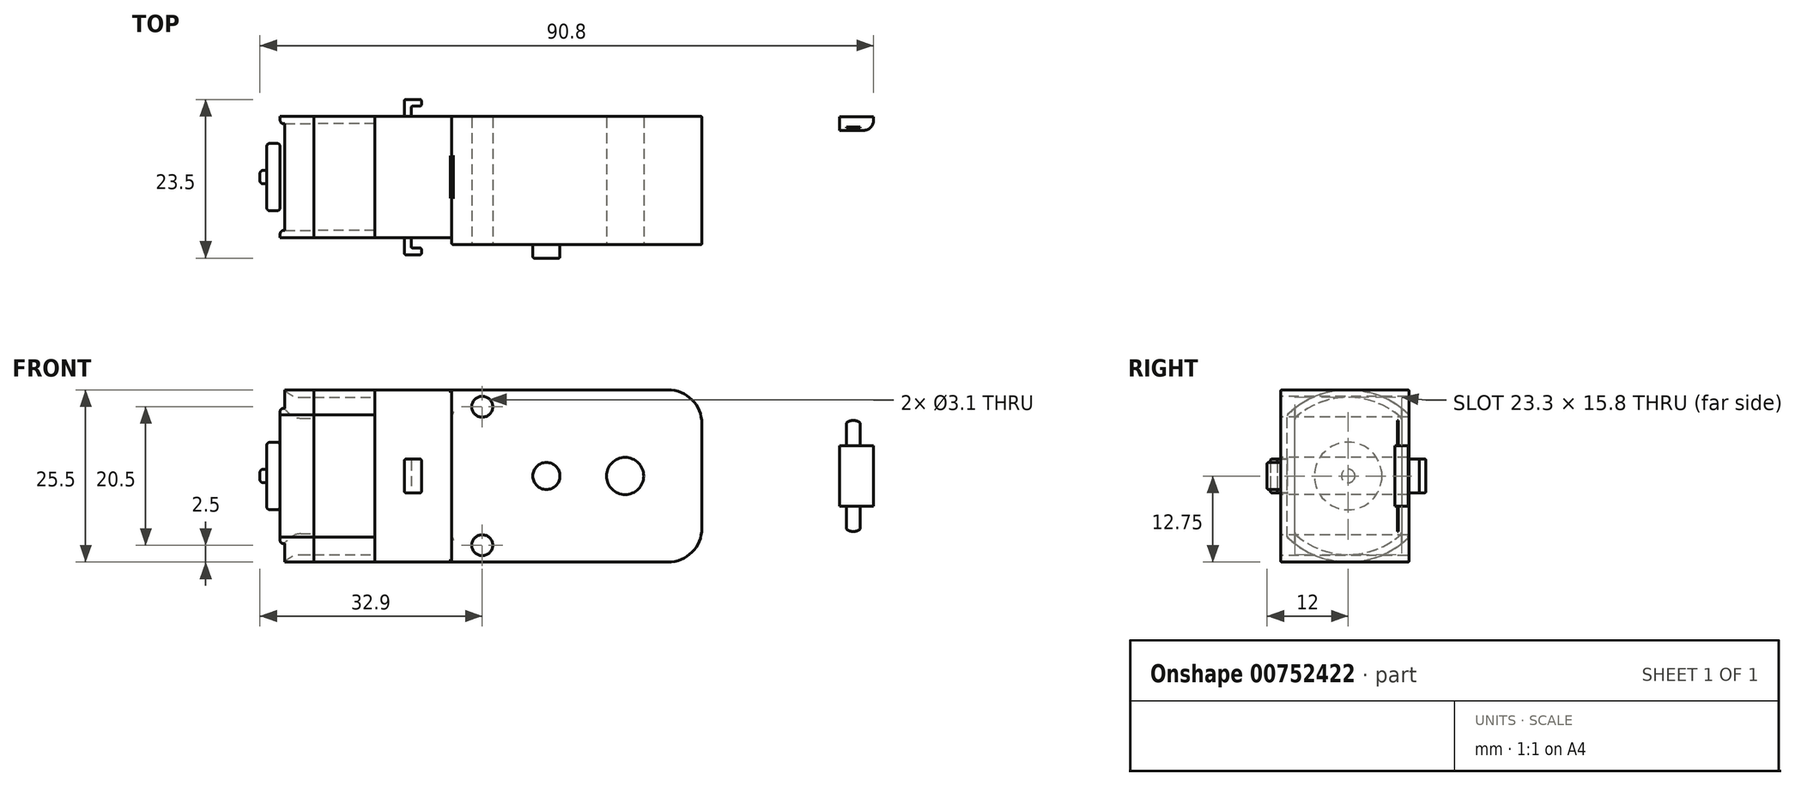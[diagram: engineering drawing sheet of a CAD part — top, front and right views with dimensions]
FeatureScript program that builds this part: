
annotation { "Feature Type Name" : "Feature", "Feature Type Description" : "" }
export const myFeature = defineFeature(function(context is Context, id is Id, definition is map)
    precondition{}
    {
        {
            var Q0;
            Q0=qCreatedBy(makeId("Front.planeOp"),FACE);
            var sketch = newSketch(context, id + "F0", { "sketchPlane" : qUnion([Q0])});
            skLineSegment(sketch, "E0.bottom", {"start": v(-18.5, 12.75) * mm, "end": v(18.5, 12.75) * mm});
            skLineSegment(sketch, "E0.top", {"start": v(-18.5, -12.75) * mm, "end": v(18.5, -12.75) * mm});
            skLineSegment(sketch, "E0.left", {"start": v(-18.5, 12.75) * mm, "end": v(-18.5, -12.75) * mm});
            skLineSegment(sketch, "E0.right", {"start": v(18.5, 12.75) * mm, "end": v(18.5, -12.75) * mm});
            skPoint(sketch, "E0.middle", {"position": v(0, 0) * mm});
            skSolve(sketch);
        }
        {
            var Q0;
            Q0=makeQuery(id+"F0.imprint","IMPRINT",FACE,{"disambiguationData":[TD([[makeQuery(id+"F0.imprint","IMPRINT",EDGE,{"derivedFrom":sQuery(id+"F0.wireOp",EDGE,"E0.bottom")}),-1.0]])]});
            extrude(context, id + "F1", {"entities" : qUnion([Q0]), "depth" : 19 * mm, "offsetDistance" : 25 * mm});
        }
        {
            var Q0;
            Q0=makeQuery(id+"F1.opExtrude","SWEPT_EDGE",EDGE,{"disambiguationData":[OSD([sQuery(id+"F0.wireOp",EDGE,"E0.bottom"),sQuery(id+"F0.wireOp",EDGE,"E0.right")])]});
            var Q1;
            Q1=makeQuery(id+"F1.opExtrude","SWEPT_EDGE",EDGE,{"disambiguationData":[OSD([sQuery(id+"F0.wireOp",EDGE,"E0.top"),sQuery(id+"F0.wireOp",EDGE,"E0.right")])]});
            fillet(context, id + "F2", {"entities" : qUnion([Q0, Q1]), "radius" : 5 * mm, "tangentPropagation" : true, "allowEdgeOverflow" : false});
        }
        {
            var Q0;
            Q0=makeQuery(id+"F1.opExtrude","SWEPT_FACE",FACE,{"disambiguationData":[OSD([sQuery(id+"F0.wireOp",EDGE,"E0.left")])]});
            var sketch = newSketch(context, id + "F3", { "sketchPlane" : qUnion([Q0])});
            skArc(sketch, "E1", {"start": v(0, 9.03) * mm, "mid": v(9, 12.75) * mm, "end": v(18, 9.03) * mm});
            skArc(sketch, "E2", {"start": v(0, -9.03) * mm, "mid": v(9, -12.75) * mm, "end": v(18, -9.03) * mm});
            skLineSegment(sketch, "E3", {"start": v(0, -9.03) * mm, "end": v(0, 9.03) * mm});
            skLineSegment(sketch, "E4", {"start": v(18, -9.03) * mm, "end": v(18, 9.03) * mm});
            skSolve(sketch);
        }
        {
            var Q0;
            {var subQ4=sQuery(id+"F3.wireOp",EDGE,"E3");Q0=makeQuery(id+"F3.imprint","IMPRINT",FACE,{"disambiguationData":[TD([[makeQuery(id+"F3.imprint","IMPRINT",EDGE,{"derivedFrom":subQ4}),1.0]])]});}
            extrude(context, id + "F4", {"entities" : qUnion([Q0]), "operationType" : NewBodyOperationType.ADD, "depth" : 11.4 * mm, "offsetDistance" : 25 * mm});
        }
        {
            var Q0;
            Q0=makeQuery(id+"F4.opExtrude","CAP_FACE",FACE,{"disambiguationData":[OSD([sQuery(id+"F3.wireOp",EDGE,"E1"),sQuery(id+"F3.wireOp",EDGE,"E2"),sQuery(id+"F3.wireOp",EDGE,"E3"),sQuery(id+"F3.wireOp",EDGE,"E4")])],"isStart":false});
            var sketch = newSketch(context, id + "F5", { "sketchPlane" : qUnion([Q0])});
            skArc(sketch, "E5.0", {"start": v(1.1, 8.56) * mm, "mid": v(9, 11.65) * mm, "end": v(16.9, 8.56) * mm});
            skLineSegment(sketch, "E5.1", {"start": v(1.1, 8.56) * mm, "end": v(1.1, -8.56) * mm});
            skArc(sketch, "E5.2", {"start": v(1.1, -8.56) * mm, "mid": v(9, -11.65) * mm, "end": v(16.9, -8.56) * mm});
            skLineSegment(sketch, "E5.3", {"start": v(16.9, -8.56) * mm, "end": v(16.9, 8.56) * mm});
            skSolve(sketch);
        }
        {
            var Q0;
            Q0=makeQuery(id+"F5.imprint","IMPRINT",FACE,{"disambiguationData":[TD([[makeQuery(id+"F5.imprint","IMPRINT",EDGE,{"derivedFrom":sQuery(id+"F5.wireOp",EDGE,"E5.0")}),-1.0]])]});
            extrude(context, id + "F6", {"entities" : qUnion([Q0]), "depth" : 9 * mm, "offsetDistance" : 25 * mm});
        }
        {
            var Q0;
            Q0=makeQuery(id+"F6.opExtrude","CAP_FACE",FACE,{"disambiguationData":[OSD([sQuery(id+"F5.wireOp",EDGE,"E5.0"),sQuery(id+"F5.wireOp",EDGE,"E5.1"),sQuery(id+"F5.wireOp",EDGE,"E5.2"),sQuery(id+"F5.wireOp",EDGE,"E5.3")])],"isStart":false});
            extrude(context, id + "F7", {"entities" : qUnion([Q0]), "depth" : 5 * mm, "offsetDistance" : 25 * mm});
        }
        {
            var Q0;
            Q0=makeQuery(id+"F7.opExtrude","CAP_EDGE",EDGE,{"disambiguationData":[OSD([sQuery(id+"F5.wireOp",EDGE,"E5.0")])],"isStart":false});
            var Q1;
            Q1=makeQuery(id+"F7.opExtrude","CAP_EDGE",EDGE,{"disambiguationData":[OSD([sQuery(id+"F5.wireOp",EDGE,"E5.2")])],"isStart":false});
            fillet(context, id + "F8", {"entities" : qUnion([Q0, Q1]), "radius" : 3 * mm, "tangentPropagation" : true, "allowEdgeOverflow" : false});
        }
        {
            var Q0;
            Q0=makeQuery(id+"F7.opExtrude","CAP_FACE",FACE,{"disambiguationData":[OSD([sQuery(id+"F5.wireOp",EDGE,"E5.0"),sQuery(id+"F5.wireOp",EDGE,"E5.1"),sQuery(id+"F5.wireOp",EDGE,"E5.2"),sQuery(id+"F5.wireOp",EDGE,"E5.3")])],"isStart":false});
            var sketch = newSketch(context, id + "F9", { "sketchPlane" : qUnion([Q0])});
            skCircle(sketch, "E6", {"center": v(9, 0) * mm, "radius": 5 * mm});
            skSolve(sketch);
        }
        {
            var Q0;
            Q0=makeQuery(id+"F9.imprint","IMPRINT",FACE,{"disambiguationData":[TD([[makeQuery(id+"F9.imprint","IMPRINT",EDGE,{"derivedFrom":sQuery(id+"F9.wireOp",EDGE,"E6")}),1.0]])]});
            extrude(context, id + "F10", {"entities" : qUnion([Q0]), "operationType" : NewBodyOperationType.ADD, "depth" : 2 * mm, "offsetDistance" : 25 * mm});
        }
        {
            var Q0;
            Q0=makeQuery(id+"F10.opExtrude","CAP_FACE",FACE,{"disambiguationData":[OSD([sQuery(id+"F9.wireOp",EDGE,"E6")])],"isStart":false});
            var sketch = newSketch(context, id + "F11", { "sketchPlane" : qUnion([Q0])});
            skCircle(sketch, "E7", {"center": v(9, 0) * mm, "radius": 1 * mm});
            skSolve(sketch);
        }
        {
            var Q0;
            Q0=makeQuery(id+"F11.imprint","IMPRINT",FACE,{"disambiguationData":[TD([[makeQuery(id+"F11.imprint","IMPRINT",EDGE,{"derivedFrom":sQuery(id+"F11.wireOp",EDGE,"E7")}),1.0]])]});
            extrude(context, id + "F12", {"entities" : qUnion([Q0]), "depth" : 1 * mm, "offsetDistance" : 25 * mm});
        }
        {
            var Q0;
            Q0=makeQuery(id+"F12.opExtrude","CAP_EDGE",EDGE,{"disambiguationData":[OSD([sQuery(id+"F11.wireOp",EDGE,"E7")])],"isStart":false});
            var Q1;
            Q1=makeQuery(id+"F10.opExtrude","CAP_EDGE",EDGE,{"disambiguationData":[OSD([sQuery(id+"F9.wireOp",EDGE,"E6")])],"isStart":false});
            var Q2;
            Q2=makeQuery(id+"F10.opExtrude","CAP_EDGE",EDGE,{"disambiguationData":[OSD([sQuery(id+"F9.wireOp",EDGE,"E6")])],"isStart":true});
            var Q3;
            Q3=makeQuery(id+"F7.opExtrude","CAP_EDGE",EDGE,{"disambiguationData":[OSD([sQuery(id+"F5.wireOp",EDGE,"E5.3")])],"isStart":false});
            var Q4;
            Q4=makeQuery(id+"F7.opExtrude","CAP_EDGE",EDGE,{"disambiguationData":[OSD([sQuery(id+"F5.wireOp",EDGE,"E5.1")])],"isStart":false});
            var Q5;
            Q5=makeQuery(id+"F6.opExtrude","SWEPT_EDGE",EDGE,{"disambiguationData":[OSD([sQuery(id+"F5.wireOp",EDGE,"E5.0"),sQuery(id+"F5.wireOp",EDGE,"E5.3")])]});
            var Q6;
            Q6=makeQuery(id+"F6.opExtrude","SWEPT_EDGE",EDGE,{"disambiguationData":[OSD([sQuery(id+"F5.wireOp",EDGE,"E5.0"),sQuery(id+"F5.wireOp",EDGE,"E5.1")])]});
            var Q7;
            Q7=makeQuery(id+"F6.opExtrude","SWEPT_EDGE",EDGE,{"disambiguationData":[OSD([sQuery(id+"F5.wireOp",EDGE,"E5.2"),sQuery(id+"F5.wireOp",EDGE,"E5.3")])]});
            var Q8;
            Q8=makeQuery(id+"F6.opExtrude","SWEPT_EDGE",EDGE,{"disambiguationData":[OSD([sQuery(id+"F5.wireOp",EDGE,"E5.1"),sQuery(id+"F5.wireOp",EDGE,"E5.2")])]});
            fillet(context, id + "F13", {"entities" : qUnion([Q0, Q1, Q2, Q3, Q4, Q5, Q6, Q7, Q8]), "radius" : 0.5 * mm, "tangentPropagation" : true, "allowEdgeOverflow" : false});
        }
        {
            var Q0;
            Q0=makeQuery(id+"F7.opExtrude","CAP_FACE",FACE,{"disambiguationData":[OSD([sQuery(id+"F5.wireOp",EDGE,"E5.0"),sQuery(id+"F5.wireOp",EDGE,"E5.1"),sQuery(id+"F5.wireOp",EDGE,"E5.2"),sQuery(id+"F5.wireOp",EDGE,"E5.3")])],"isStart":false});
            var sketch = newSketch(context, id + "F14", { "sketchPlane" : qUnion([Q0])});
            skArc(sketch, "E8", {"start": v(7.5, 9.65) * mm, "mid": v(9, 8.15) * mm, "end": v(10.5, 9.65) * mm});
            skArc(sketch, "E9", {"start": v(7.5, 11.55) * mm, "mid": v(9, 11.65) * mm, "end": v(10.5, 11.55) * mm});
            skLineSegment(sketch, "E10", {"start": v(7.5, 9.65) * mm, "end": v(7.5, 11.55) * mm});
            skLineSegment(sketch, "E11", {"start": v(10.5, 9.65) * mm, "end": v(10.5, 11.55) * mm});
            skLineSegment(sketch, "E12.MirrorCS", {"start": v(10.5, -9.65) * mm, "end": v(10.5, -11.55) * mm});
            skArc(sketch, "E13.MirrorCS", {"start": v(7.5, -9.65) * mm, "mid": v(9, -8.15) * mm, "end": v(10.5, -9.65) * mm});
            skLineSegment(sketch, "E14.MirrorCS", {"start": v(7.5, -9.65) * mm, "end": v(7.5, -11.55) * mm});
            skArc(sketch, "E15.MirrorCS", {"start": v(7.5, -11.55) * mm, "mid": v(9, -11.65) * mm, "end": v(10.5, -11.55) * mm});
            skSolve(sketch);
        }
        {
            var Q0;
            Q0=makeQuery(id+"F14.imprint","IMPRINT",FACE,{"disambiguationData":[TD([[makeQuery(id+"F14.imprint","IMPRINT",EDGE,{"derivedFrom":sQuery(id+"F14.wireOp",EDGE,"E9")}),-1.0]])]});
            var Q1;
            {var subQ0=sQuery(id+"F14.wireOp",EDGE,"E8");var subQ1=sQuery(id+"F5.wireOp",EDGE,"E5.0");var subQ2=makeQuery(id+"F8.opFillet","BLEND_EDGE",EDGE,{"blendedFrom":[makeQuery(id+"F7.opExtrude","CAP_EDGE",EDGE,{"disambiguationData":[OSD([subQ1])],"isStart":false}),makeQuery(id+"F7.opExtrude","CAP_FACE",FACE,{"disambiguationData":[OSD([subQ1,sQuery(id+"F5.wireOp",EDGE,"E5.1"),sQuery(id+"F5.wireOp",EDGE,"E5.2"),sQuery(id+"F5.wireOp",EDGE,"E5.3")])],"isStart":false})],"blendedInto":[makeQuery(id+"F7.opExtrude","CAP_FACE",FACE,{"disambiguationData":[OSD([subQ1,sQuery(id+"F5.wireOp",EDGE,"E5.1"),sQuery(id+"F5.wireOp",EDGE,"E5.2"),sQuery(id+"F5.wireOp",EDGE,"E5.3")])],"isStart":false})]});var subQ3=makeQuery(id+"F14.imprint","INTERSECT",VERTEX,{"disambiguationData":[OD(0.0)],"derivedFrom":[subQ2,subQ0]});Q1=makeQuery(id+"F14.imprint","IMPRINT",FACE,{"disambiguationData":[TD([[makeQuery(id+"F14.imprint","IMPRINT",EDGE,{"disambiguationData":[TD([[subQ3,-1.0]])],"derivedFrom":subQ0}),1.0]])]});}
            var Q2;
            {var subQ2=sQuery(id+"F14.wireOp",EDGE,"E12.MirrorCS");Q2=makeQuery(id+"F14.imprint","IMPRINT",FACE,{"disambiguationData":[TD([[makeQuery(id+"F14.imprint","IMPRINT",EDGE,{"derivedFrom":subQ2}),-1.0]])]});}
            var Q3;
            {var subQ0=sQuery(id+"F14.wireOp",EDGE,"E13.MirrorCS");var subQ1=sQuery(id+"F5.wireOp",EDGE,"E5.2");var subQ2=makeQuery(id+"F8.opFillet","BLEND_EDGE",EDGE,{"blendedFrom":[makeQuery(id+"F7.opExtrude","CAP_EDGE",EDGE,{"disambiguationData":[OSD([subQ1])],"isStart":false}),makeQuery(id+"F7.opExtrude","CAP_FACE",FACE,{"disambiguationData":[OSD([sQuery(id+"F5.wireOp",EDGE,"E5.0"),sQuery(id+"F5.wireOp",EDGE,"E5.1"),subQ1,sQuery(id+"F5.wireOp",EDGE,"E5.3")])],"isStart":false})],"blendedInto":[makeQuery(id+"F7.opExtrude","CAP_FACE",FACE,{"disambiguationData":[OSD([sQuery(id+"F5.wireOp",EDGE,"E5.0"),sQuery(id+"F5.wireOp",EDGE,"E5.1"),subQ1,sQuery(id+"F5.wireOp",EDGE,"E5.3")])],"isStart":false})]});var subQ3=makeQuery(id+"F14.imprint","INTERSECT",VERTEX,{"disambiguationData":[OD(0.0)],"derivedFrom":[subQ2,subQ0]});Q3=makeQuery(id+"F14.imprint","IMPRINT",FACE,{"disambiguationData":[TD([[makeQuery(id+"F14.imprint","IMPRINT",EDGE,{"disambiguationData":[TD([[subQ3,-1.0]])],"derivedFrom":subQ0}),-1.0]])]});}
            extrude(context, id + "F15", {"entities" : qUnion([Q0, Q1, Q2, Q3]), "operationType" : NewBodyOperationType.REMOVE, "oppositeDirection" : true, "depth" : 6 * mm, "offsetDistance" : 25 * mm});
        }
        {
            var Q0;
            Q0=makeQuery(id+"F7.opExtrude","SWEPT_FACE",FACE,{"disambiguationData":[OSD([sQuery(id+"F5.wireOp",EDGE,"E5.1")])]});
            var sketch = newSketch(context, id + "F16", { "sketchPlane" : qUnion([Q0])});
            skLineSegment(sketch, "E16", {"start": v(38.9, -4.5) * mm, "end": v(38.9, 4.5) * mm});
            skLineSegment(sketch, "E17", {"start": v(38.9, 4.5) * mm, "end": v(43.9, 4.5) * mm});
            skLineSegment(sketch, "E18", {"start": v(43.9, 4.5) * mm, "end": v(43.9, -4.5) * mm});
            skLineSegment(sketch, "E19", {"start": v(43.9, -4.5) * mm, "end": v(38.9, -4.5) * mm});
            skSolve(sketch);
        }
        {
            var Q0;
            {var subQ5=sQuery(id+"F16.wireOp",EDGE,"E16");Q0=makeQuery(id+"F16.imprint","IMPRINT",FACE,{"disambiguationData":[TD([[makeQuery(id+"F16.imprint","IMPRINT",EDGE,{"derivedFrom":subQ5}),1.0]])]});}
            var Q1;
            {var subQ1=sQuery(id+"F16.wireOp",EDGE,"E18");Q1=makeQuery(id+"F16.imprint","IMPRINT",FACE,{"disambiguationData":[TD([[makeQuery(id+"F16.imprint","IMPRINT",EDGE,{"derivedFrom":subQ1}),-1.0]])]});}
            extrude(context, id + "F17", {"entities" : qUnion([Q0, Q1]), "endBound" : BoundingType.SYMMETRIC, "depth" : 2 * mm, "offsetDistance" : 25 * mm});
        }
        {
            var Q0;
            Q0=makeQuery(id+"F17.opExtrude","CAP_EDGE",EDGE,{"disambiguationData":[OSD([sQuery(id+"F16.wireOp",EDGE,"E18")])],"isStart":false});
            fillet(context, id + "F18", {"entities" : qUnion([Q0]), "radius" : 1.5 * mm, "tangentPropagation" : true, "allowEdgeOverflow" : false});
        }
        {
            var Q0;
            Q0=makeQuery(id+"F7.opExtrude","SWEPT_FACE",FACE,{"disambiguationData":[OSD([sQuery(id+"F5.wireOp",EDGE,"E5.1")])]});
            cPlane(context, id + "F19", {"entities" : qUnion([Q0]), "cplaneType" : CPlaneType.OFFSET, "offset" : 0.5 * mm, "width" : 150 * mm, "height" : 150 * mm});
        }
        {
            var Q0;
            Q0=qCreatedBy(id+"F19.planeOp",FACE);
            var sketch = newSketch(context, id + "F20", { "sketchPlane" : qUnion([Q0])});
            skLineSegment(sketch, "E20.bottom", {"start": v(39.9, 4.5) * mm, "end": v(41.9, 4.5) * mm});
            skLineSegment(sketch, "E20.left", {"start": v(39.9, 4.5) * mm, "end": v(39.9, 7.85) * mm});
            skLineSegment(sketch, "E20.right", {"start": v(41.9, 4.5) * mm, "end": v(41.9, 7.85) * mm});
            skArc(sketch, "E21", {"start": v(41.9, 7.85) * mm, "mid": v(40.9, 8.23) * mm, "end": v(39.9, 7.85) * mm});
            skLineSegment(sketch, "E22.MirrorCS", {"start": v(39.9, -4.5) * mm, "end": v(41.9, -4.5) * mm});
            skLineSegment(sketch, "E23.MirrorCS", {"start": v(39.9, -4.5) * mm, "end": v(39.9, -7.85) * mm});
            skArc(sketch, "E24.MirrorCS", {"start": v(41.9, -7.85) * mm, "mid": v(40.9, -8.23) * mm, "end": v(39.9, -7.85) * mm});
            skLineSegment(sketch, "E25.MirrorCS", {"start": v(41.9, -4.5) * mm, "end": v(41.9, -7.85) * mm});
            skSolve(sketch);
        }
        {
            var Q0;
            Q0=makeQuery(id+"F20.imprint","IMPRINT",FACE,{"disambiguationData":[TD([[makeQuery(id+"F20.imprint","IMPRINT",EDGE,{"derivedFrom":sQuery(id+"F20.wireOp",EDGE,"E20.bottom")}),1.0]])]});
            var Q1;
            Q1=makeQuery(id+"F20.imprint","IMPRINT",FACE,{"disambiguationData":[TD([[makeQuery(id+"F20.imprint","IMPRINT",EDGE,{"derivedFrom":sQuery(id+"F20.wireOp",EDGE,"E22.MirrorCS")}),-1.0]])]});
            extrude(context, id + "F21", {"entities" : qUnion([Q0, Q1]), "depth" : 0.1 * mm, "offsetDistance" : 25 * mm});
        }
        {
            var Q0;
            Q0=makeQuery(id+"F1.opExtrude","CAP_FACE",FACE,{"disambiguationData":[OSD([sQuery(id+"F0.wireOp",EDGE,"E0.bottom"),sQuery(id+"F0.wireOp",EDGE,"E0.top"),sQuery(id+"F0.wireOp",EDGE,"E0.left"),sQuery(id+"F0.wireOp",EDGE,"E0.right")])],"isStart":false});
            var sketch = newSketch(context, id + "F22", { "sketchPlane" : qUnion([Q0])});
            skCircle(sketch, "E26", {"center": v(-4.5, 0) * mm, "radius": 2 * mm});
            skSolve(sketch);
        }
        {
            var Q0;
            Q0=makeQuery(id+"F22.imprint","IMPRINT",FACE,{"disambiguationData":[TD([[makeQuery(id+"F22.imprint","IMPRINT",EDGE,{"derivedFrom":sQuery(id+"F22.wireOp",EDGE,"E26")}),1.0]])]});
            extrude(context, id + "F23", {"entities" : qUnion([Q0]), "operationType" : NewBodyOperationType.ADD, "depth" : 2 * mm, "offsetDistance" : 25 * mm});
        }
        {
            var Q0;
            Q0=makeQuery(id+"F1.opExtrude","CAP_FACE",FACE,{"disambiguationData":[OSD([sQuery(id+"F0.wireOp",EDGE,"E0.bottom"),sQuery(id+"F0.wireOp",EDGE,"E0.top"),sQuery(id+"F0.wireOp",EDGE,"E0.left"),sQuery(id+"F0.wireOp",EDGE,"E0.right")])],"isStart":false});
            var sketch = newSketch(context, id + "F24", { "sketchPlane" : qUnion([Q0])});
            skCircle(sketch, "E27", {"center": v(7.15, 0) * mm, "radius": 2.75 * mm});
            skPoint(sketch, "E28", {"position": v(-14, 10.25) * mm});
            skPoint(sketch, "E29", {"position": v(-14, -10.25) * mm});
            skSolve(sketch);
        }
        {
            var Q0;
            Q0=makeQuery(id+"F24.imprint","IMPRINT",FACE,{"disambiguationData":[TD([[makeQuery(id+"F24.imprint","IMPRINT",EDGE,{"derivedFrom":sQuery(id+"F24.wireOp",EDGE,"E27")}),1.0]])]});
            extrude(context, id + "F25", {"entities" : qUnion([Q0]), "operationType" : NewBodyOperationType.REMOVE, "endBound" : BoundingType.THROUGH_ALL, "oppositeDirection" : true, "depth" : 25 * mm, "offsetDistance" : 25 * mm});
        }
        {
            var Q0;
            Q0=sQuery(id+"F24.wireOp",VERTEX,"E28");
            var Q1;
            Q1=sQuery(id+"F24.wireOp",VERTEX,"E29");
            var Q2;
            Q2=makeQuery(id+"F1.opExtrude","SWEPT_BODY",BODY,{"disambiguationData":[OSD([sQuery(id+"F0.wireOp",EDGE,"E0.bottom"),sQuery(id+"F0.wireOp",EDGE,"E0.top"),sQuery(id+"F0.wireOp",EDGE,"E0.left"),sQuery(id+"F0.wireOp",EDGE,"E0.right")])]});
            hole(context, id + "F26", {"style" : HoleStyle.SIMPLE, "endStyle" : HoleEndStyle.THROUGH, "holeDiameter" : 3.1 * mm, "majorDiameter" : 5 * mm, "isTappedThrough" : true, "tappedDepth" : 12 * mm, "tapClearance" : 3, "locations" : qUnion([Q0, Q1]), "scope" : qUnion([Q2])});
        }
        {
            var Q0;
            Q0=qCreatedBy(makeId("Top.planeOp"),FACE);
            var sketch = newSketch(context, id + "F27", { "sketchPlane" : qUnion([Q0])});
            skLineSegment(sketch, "E30", {"start": v(-25.5, -18) * mm, "end": v(-25.5, -20.5) * mm});
            skLineSegment(sketch, "E31", {"start": v(-25.5, -20.5) * mm, "end": v(-23, -20.5) * mm});
            skLineSegment(sketch, "E32", {"start": v(-23, -20.5) * mm, "end": v(-23, -19.5) * mm});
            skLineSegment(sketch, "E33", {"start": v(-23, -19.5) * mm, "end": v(-24.5, -19.5) * mm});
            skLineSegment(sketch, "E34", {"start": v(-24.5, -19.5) * mm, "end": v(-24.5, -18) * mm});
            skLineSegment(sketch, "E35", {"start": v(-24.5, -18) * mm, "end": v(-25.5, -18) * mm});
            skLineSegment(sketch, "E36", {"start": v(-36.83, -9) * mm, "end": v(-23.9, -9) * mm});
            skLineSegment(sketch, "E37.MirrorCS", {"start": v(-24.5, 0) * mm, "end": v(-25.5, 0) * mm});
            skLineSegment(sketch, "E38.MirrorCS", {"start": v(-24.5, 1.5) * mm, "end": v(-24.5, 0) * mm});
            skLineSegment(sketch, "E39.MirrorCS", {"start": v(-23, 1.5) * mm, "end": v(-24.5, 1.5) * mm});
            skLineSegment(sketch, "E40.MirrorCS", {"start": v(-25.5, 0) * mm, "end": v(-25.5, 2.5) * mm});
            skLineSegment(sketch, "E41.MirrorCS", {"start": v(-23, 2.5) * mm, "end": v(-23, 1.5) * mm});
            skLineSegment(sketch, "E42.MirrorCS", {"start": v(-25.5, 2.5) * mm, "end": v(-23, 2.5) * mm});
            skSolve(sketch);
        }
        {
            var Q0;
            Q0=makeQuery(id+"F27.imprint","IMPRINT",FACE,{"disambiguationData":[TD([[makeQuery(id+"F27.imprint","IMPRINT",EDGE,{"derivedFrom":sQuery(id+"F27.wireOp",EDGE,"E30")}),1.0]])]});
            var Q1;
            Q1=makeQuery(id+"F27.imprint","IMPRINT",FACE,{"disambiguationData":[TD([[makeQuery(id+"F27.imprint","IMPRINT",EDGE,{"derivedFrom":sQuery(id+"F27.wireOp",EDGE,"E37.MirrorCS")}),-1.0]])]});
            extrude(context, id + "F28", {"entities" : qUnion([Q0, Q1]), "operationType" : NewBodyOperationType.ADD, "endBound" : BoundingType.SYMMETRIC, "depth" : 5 * mm, "offsetDistance" : 25 * mm});
        }
        {
            var Q0;
            Q0=makeQuery(id+"F4.boolean.opBoolean","MERGE",FACE,{"derivedFrom":[makeQuery(id+"F1.opExtrude","CAP_FACE",FACE,{"disambiguationData":[OSD([sQuery(id+"F0.wireOp",EDGE,"E0.bottom"),sQuery(id+"F0.wireOp",EDGE,"E0.top"),sQuery(id+"F0.wireOp",EDGE,"E0.left"),sQuery(id+"F0.wireOp",EDGE,"E0.right")])],"isStart":true}),makeQuery(id+"F4.opExtrude","SWEPT_FACE",FACE,{"disambiguationData":[OSD([sQuery(id+"F3.wireOp",EDGE,"E3")])]})]});
            var Q1;
            Q1=makeQuery(id+"F1.opExtrude","CAP_FACE",FACE,{"disambiguationData":[OSD([sQuery(id+"F0.wireOp",EDGE,"E0.bottom"),sQuery(id+"F0.wireOp",EDGE,"E0.top"),sQuery(id+"F0.wireOp",EDGE,"E0.left"),sQuery(id+"F0.wireOp",EDGE,"E0.right")])],"isStart":false});
            var Q2;
            Q2=makeQuery(id+"F4.opExtrude","SWEPT_FACE",FACE,{"disambiguationData":[OSD([sQuery(id+"F3.wireOp",EDGE,"E4")])]});
            var Q3;
            Q3=makeQuery(id+"F4.opExtrude","SWEPT_FACE",FACE,{"disambiguationData":[OSD([sQuery(id+"F3.wireOp",EDGE,"E1")])]});
            var Q4;
            Q4=makeQuery(id+"F4.opExtrude","SWEPT_FACE",FACE,{"disambiguationData":[OSD([sQuery(id+"F3.wireOp",EDGE,"E2")])]});
            var Q5;
            Q5=makeQuery(id+"F28.opExtrude","SWEPT_FACE",FACE,{"disambiguationData":[OSD([sQuery(id+"F27.wireOp",EDGE,"E42.MirrorCS")])]});
            var Q6;
            Q6=makeQuery(id+"F28.opExtrude","CAP_FACE",FACE,{"disambiguationData":[OSD([sQuery(id+"F27.wireOp",EDGE,"E37.MirrorCS"),sQuery(id+"F27.wireOp",EDGE,"E38.MirrorCS"),sQuery(id+"F27.wireOp",EDGE,"E39.MirrorCS"),sQuery(id+"F27.wireOp",EDGE,"E40.MirrorCS"),sQuery(id+"F27.wireOp",EDGE,"E41.MirrorCS"),sQuery(id+"F27.wireOp",EDGE,"E42.MirrorCS")])],"isStart":false});
            var Q7;
            Q7=makeQuery(id+"F28.opExtrude","CAP_FACE",FACE,{"disambiguationData":[OSD([sQuery(id+"F27.wireOp",EDGE,"E37.MirrorCS"),sQuery(id+"F27.wireOp",EDGE,"E38.MirrorCS"),sQuery(id+"F27.wireOp",EDGE,"E39.MirrorCS"),sQuery(id+"F27.wireOp",EDGE,"E40.MirrorCS"),sQuery(id+"F27.wireOp",EDGE,"E41.MirrorCS"),sQuery(id+"F27.wireOp",EDGE,"E42.MirrorCS")])],"isStart":true});
            var Q8;
            Q8=makeQuery(id+"F28.opExtrude","SWEPT_FACE",FACE,{"disambiguationData":[OSD([sQuery(id+"F27.wireOp",EDGE,"E39.MirrorCS")])]});
            var Q9;
            {var subQ0=sQuery(id+"F0.wireOp",EDGE,"E0.left");var subQ1=sQuery(id+"F0.wireOp",EDGE,"E0.top");Q9=makeQuery(id+"F4.boolean.opBoolean","SPLIT",EDGE,{"disambiguationData":[TD([makeQuery(id+"F1.opExtrude","CAP_FACE",FACE,{"disambiguationData":[OSD([sQuery(id+"F0.wireOp",EDGE,"E0.bottom"),subQ1,subQ0,sQuery(id+"F0.wireOp",EDGE,"E0.right")])],"isStart":false})])],"derivedFrom":makeQuery(id+"F1.opExtrude","SWEPT_EDGE",EDGE,{"disambiguationData":[OSD([subQ1,subQ0])]})});}
            var Q10;
            {var subQ0=sQuery(id+"F0.wireOp",EDGE,"E0.left");var subQ1=sQuery(id+"F0.wireOp",EDGE,"E0.top");Q10=makeQuery(id+"F4.boolean.opBoolean","SPLIT",EDGE,{"disambiguationData":[TD([makeQuery(id+"F4.opExtrude","SWEPT_FACE",FACE,{"disambiguationData":[OSD([sQuery(id+"F3.wireOp",EDGE,"E3")])]})])],"derivedFrom":makeQuery(id+"F1.opExtrude","SWEPT_EDGE",EDGE,{"disambiguationData":[OSD([subQ1,subQ0])]})});}
            var Q11;
            {var subQ0=sQuery(id+"F0.wireOp",EDGE,"E0.bottom");var subQ1=sQuery(id+"F0.wireOp",EDGE,"E0.left");Q11=makeQuery(id+"F4.boolean.opBoolean","SPLIT",EDGE,{"disambiguationData":[TD([makeQuery(id+"F1.opExtrude","CAP_FACE",FACE,{"disambiguationData":[OSD([subQ0,sQuery(id+"F0.wireOp",EDGE,"E0.top"),subQ1,sQuery(id+"F0.wireOp",EDGE,"E0.right")])],"isStart":false})])],"derivedFrom":makeQuery(id+"F1.opExtrude","SWEPT_EDGE",EDGE,{"disambiguationData":[OSD([subQ0,subQ1])]})});}
            var Q12;
            {var subQ0=sQuery(id+"F0.wireOp",EDGE,"E0.left");var subQ1=sQuery(id+"F0.wireOp",EDGE,"E0.bottom");Q12=makeQuery(id+"F4.boolean.opBoolean","SPLIT",EDGE,{"disambiguationData":[TD([makeQuery(id+"F4.opExtrude","SWEPT_FACE",FACE,{"disambiguationData":[OSD([sQuery(id+"F3.wireOp",EDGE,"E3")])]})])],"derivedFrom":makeQuery(id+"F1.opExtrude","SWEPT_EDGE",EDGE,{"disambiguationData":[OSD([subQ1,subQ0])]})});}
            var Q13;
            Q13=makeQuery(id+"F28.opExtrude","CAP_FACE",FACE,{"disambiguationData":[OSD([sQuery(id+"F27.wireOp",EDGE,"E30"),sQuery(id+"F27.wireOp",EDGE,"E31"),sQuery(id+"F27.wireOp",EDGE,"E32"),sQuery(id+"F27.wireOp",EDGE,"E33"),sQuery(id+"F27.wireOp",EDGE,"E34"),sQuery(id+"F27.wireOp",EDGE,"E35")])],"isStart":false});
            var Q14;
            Q14=makeQuery(id+"F28.opExtrude","CAP_FACE",FACE,{"disambiguationData":[OSD([sQuery(id+"F27.wireOp",EDGE,"E30"),sQuery(id+"F27.wireOp",EDGE,"E31"),sQuery(id+"F27.wireOp",EDGE,"E32"),sQuery(id+"F27.wireOp",EDGE,"E33"),sQuery(id+"F27.wireOp",EDGE,"E34"),sQuery(id+"F27.wireOp",EDGE,"E35")])],"isStart":true});
            var Q15;
            Q15=makeQuery(id+"F28.opExtrude","SWEPT_EDGE",EDGE,{"disambiguationData":[OSD([sQuery(id+"F27.wireOp",EDGE,"E30"),sQuery(id+"F27.wireOp",EDGE,"E31")])]});
            var Q16;
            Q16=makeQuery(id+"F28.opExtrude","SWEPT_EDGE",EDGE,{"disambiguationData":[OSD([sQuery(id+"F27.wireOp",EDGE,"E31"),sQuery(id+"F27.wireOp",EDGE,"E32")])]});
            var Q17;
            Q17=makeQuery(id+"F28.opExtrude","SWEPT_EDGE",EDGE,{"disambiguationData":[OSD([sQuery(id+"F27.wireOp",EDGE,"E32"),sQuery(id+"F27.wireOp",EDGE,"E33")])]});
            var Q18;
            Q18=makeQuery(id+"F28.opExtrude","SWEPT_EDGE",EDGE,{"disambiguationData":[OSD([sQuery(id+"F27.wireOp",EDGE,"E33"),sQuery(id+"F27.wireOp",EDGE,"E34")])]});
            var Q19;
            Q19=makeQuery(id+"F23.opExtrude","CAP_EDGE",EDGE,{"disambiguationData":[OSD([sQuery(id+"F22.wireOp",EDGE,"E26")])],"isStart":false});
            fillet(context, id + "F29", {"entities" : qUnion([Q0, Q1, Q2, Q3, Q4, Q5, Q6, Q7, Q8, Q9, Q10, Q11, Q12, Q13, Q14, Q15, Q16, Q17, Q18, Q19]), "radius" : 0.2 * mm, "tangentPropagation" : true, "allowEdgeOverflow" : false});
        }
    });
